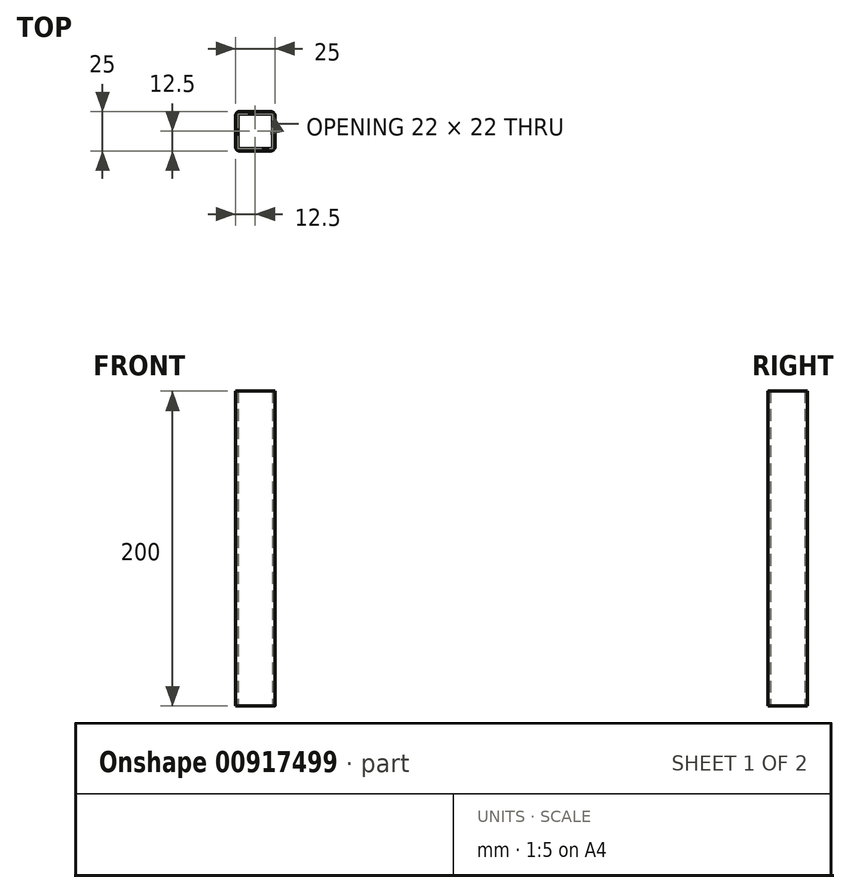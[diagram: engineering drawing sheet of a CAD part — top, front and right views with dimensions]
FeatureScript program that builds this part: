
annotation { "Feature Type Name" : "Feature", "Feature Type Description" : "" }
export const myFeature = defineFeature(function(context is Context, id is Id, definition is map)
    precondition{}
    {
        {
            var Q0;
            Q0=qCreatedBy(makeId("Top.planeOp"),FACE);
            var sketch = newSketch(context, id + "F0", { "sketchPlane" : qUnion([Q0])});
            skLineSegment(sketch, "E0.bottom", {"start": v(10, 12.5) * mm, "end": v(-10, 12.5) * mm});
            skLineSegment(sketch, "E0.top", {"start": v(10, -12.5) * mm, "end": v(-10, -12.5) * mm});
            skLineSegment(sketch, "E0.left", {"start": v(12.5, 10) * mm, "end": v(12.5, -10) * mm});
            skLineSegment(sketch, "E0.right", {"start": v(-12.5, 10) * mm, "end": v(-12.5, -10) * mm});
            skPoint(sketch, "E0.middle", {"position": v(0, 0) * mm});
            skPoint(sketch, "E1.visualSharp", {"position": v(-12.5, 12.5) * mm});
            skArc(sketch, "E1.filletArc", {"start": v(-10, 12.5) * mm, "mid": v(-11.77, 11.77) * mm, "end": v(-12.5, 10) * mm});
            skPoint(sketch, "E2.visualSharp", {"position": v(12.5, 12.5) * mm});
            skArc(sketch, "E2.filletArc", {"start": v(12.5, 10) * mm, "mid": v(11.77, 11.77) * mm, "end": v(10, 12.5) * mm});
            skPoint(sketch, "E3.visualSharp", {"position": v(12.5, -12.5) * mm});
            skArc(sketch, "E3.filletArc", {"start": v(10, -12.5) * mm, "mid": v(11.77, -11.77) * mm, "end": v(12.5, -10) * mm});
            skPoint(sketch, "E4.visualSharp", {"position": v(-12.5, -12.5) * mm});
            skArc(sketch, "E4.filletArc", {"start": v(-12.5, -10) * mm, "mid": v(-11.77, -11.77) * mm, "end": v(-10, -12.5) * mm});
            skLineSegment(sketch, "E5.0", {"start": v(10, -11) * mm, "end": v(-10, -11) * mm});
            skLineSegment(sketch, "E5.1", {"start": v(11, 11) * mm, "end": v(11, -10) * mm});
            skLineSegment(sketch, "E5.2", {"start": v(11, 11) * mm, "end": v(-10, 11) * mm});
            skLineSegment(sketch, "E5.3", {"start": v(-11, 10) * mm, "end": v(-11, -10) * mm});
            skPoint(sketch, "E6.visualSharp", {"position": v(-11, -11) * mm});
            skArc(sketch, "E6.filletArc", {"start": v(-11, -10) * mm, "mid": v(-10.7, -10.7) * mm, "end": v(-10, -11) * mm});
            skPoint(sketch, "E7.visualSharp", {"position": v(-11, 11) * mm});
            skArc(sketch, "E7.filletArc", {"start": v(-10, 11) * mm, "mid": v(-10.7, 10.7) * mm, "end": v(-11, 10) * mm});
            skPoint(sketch, "E8.visualSharp", {"position": v(11, -11) * mm});
            skArc(sketch, "E8.filletArc", {"start": v(10, -11) * mm, "mid": v(10.7, -10.7) * mm, "end": v(11, -10) * mm});
            skSolve(sketch);
        }
        {
            var Q0;
            Q0=qSketchRegion(id+"F0",true);
            extrude(context, id + "F1", {"entities" : qUnion([Q0]), "depth" : 200 * mm, "offsetDistance" : 25 * mm});
        }
    });
